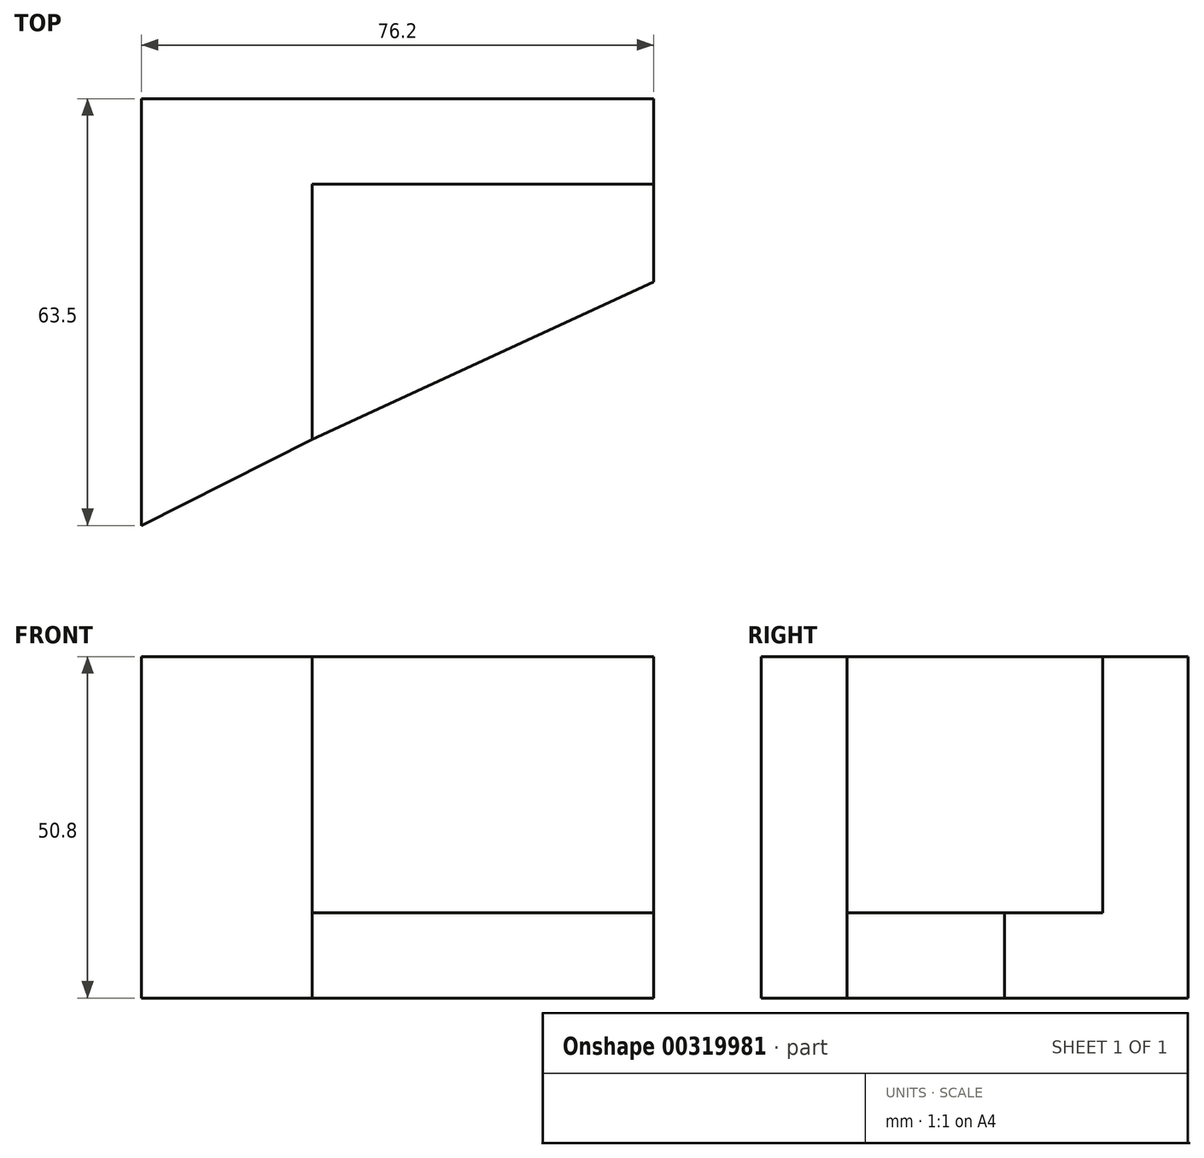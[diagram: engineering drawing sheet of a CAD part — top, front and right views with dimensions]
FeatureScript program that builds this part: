
annotation { "Feature Type Name" : "Feature", "Feature Type Description" : "" }
export const myFeature = defineFeature(function(context is Context, id is Id, definition is map)
    precondition{}
    {
        {
            var Q0;
            Q0=qCreatedBy(makeId("Top.planeOp"),FACE);
            var sketch = newSketch(context, id + "F0", { "sketchPlane" : qUnion([Q0])});
            skLineSegment(sketch, "E0", {"start": v(0, 0) * mm, "end": v(0, 63.5) * mm});
            skLineSegment(sketch, "E1", {"start": v(0, 63.5) * mm, "end": v(25.4, 63.5) * mm});
            skLineSegment(sketch, "E2", {"start": v(25.4, 63.5) * mm, "end": v(25.4, 12.78) * mm});
            skLineSegment(sketch, "E3", {"start": v(0, 0) * mm, "end": v(25.4, 12.78) * mm});
            skLineSegment(sketch, "E4.bottom", {"start": v(25.4, 63.5) * mm, "end": v(76.2, 63.5) * mm});
            skLineSegment(sketch, "E4.top", {"start": v(25.4, 63.5) * mm, "end": v(76.2, 63.5) * mm});
            skLineSegment(sketch, "E4.left", {"start": v(25.4, 63.5) * mm, "end": v(25.4, 63.5) * mm});
            skLineSegment(sketch, "E4.right", {"start": v(76.2, 63.5) * mm, "end": v(76.2, 63.5) * mm});
            skLineSegment(sketch, "E5", {"start": v(76.2, 63.5) * mm, "end": v(76.2, 50.8) * mm});
            skLineSegment(sketch, "E6", {"start": v(76.2, 50.8) * mm, "end": v(25.4, 50.8) * mm});
            skLineSegment(sketch, "E7", {"start": v(25.4, 50.8) * mm, "end": v(25.4, 63.5) * mm});
            skSolve(sketch);
        }
        {
            var Q0;
            Q0 = qSketchRegion(id + "F0", true);
            extrude(context, id + "F1", {"entities" : qUnion([Q0]), "depth" : 50.8 * mm});
        }
        {
            var Q0;
            Q0=makeQuery(id+"F1.opExtrude","CAP_FACE",FACE,{"disambiguationData":[OSD([sQuery(id+"F0.wireOp",EDGE,"E0"),sQuery(id+"F0.wireOp",EDGE,"E1"),sQuery(id+"F0.wireOp",EDGE,"E2"),sQuery(id+"F0.wireOp",EDGE,"E3"),sQuery(id+"F0.wireOp",EDGE,"E4.top"),sQuery(id+"F0.wireOp",EDGE,"E5"),sQuery(id+"F0.wireOp",EDGE,"E6")])],"isStart":true});
            var sketch = newSketch(context, id + "F2", { "sketchPlane" : qUnion([Q0])});
            skLineSegment(sketch, "E8", {"start": v(25.4, -12.78) * mm, "end": v(76.2, -36.21) * mm});
            skLineSegment(sketch, "E9", {"start": v(76.2, -36.21) * mm, "end": v(76.2, -50.8) * mm});
            skLineSegment(sketch, "E10", {"start": v(76.2, -50.8) * mm, "end": v(25.4, -50.8) * mm});
            skLineSegment(sketch, "E11", {"start": v(25.4, -50.8) * mm, "end": v(25.4, -12.78) * mm});
            skSolve(sketch);
        }
        {
            var Q0;
            Q0 = qSketchRegion(id + "F2", true);
            extrude(context, id + "F3", {"entities" : qUnion([Q0]), "operationType" : NewBodyOperationType.ADD, "oppositeDirection" : true, "depth" : 12.7 * mm});
        }
    });
